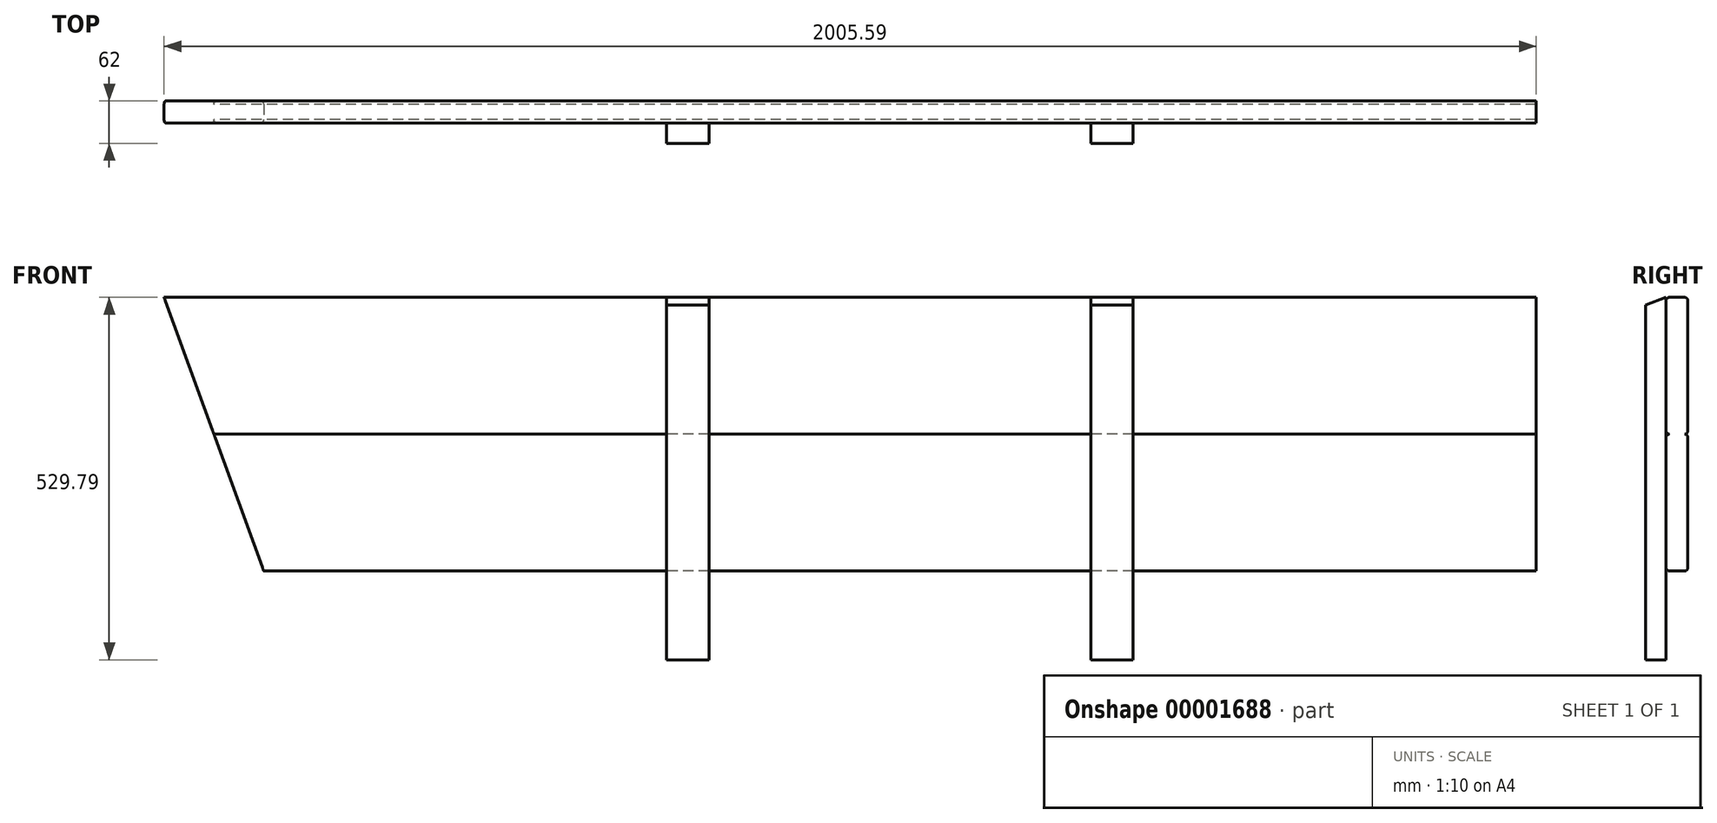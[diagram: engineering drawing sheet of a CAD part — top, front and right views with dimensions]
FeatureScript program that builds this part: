
annotation { "Feature Type Name" : "Feature", "Feature Type Description" : "" }
export const myFeature = defineFeature(function(context is Context, id is Id, definition is map)
    precondition{}
    {
        {
            var Q0;
            Q0=qCreatedBy(makeId("Right.planeOp"),FACE);
            var sketch = newSketch(context, id + "F0", { "sketchPlane" : qUnion([Q0])});
            skLineSegment(sketch, "E0.bottom", {"start": v(5, 0) * mm, "end": v(27, 0) * mm});
            skLineSegment(sketch, "E0.top", {"start": v(5, 200) * mm, "end": v(27, 200) * mm});
            skLineSegment(sketch, "E0.left", {"start": v(0, 5) * mm, "end": v(0, 195) * mm});
            skLineSegment(sketch, "E0.right", {"start": v(32, 5) * mm, "end": v(32, 195) * mm});
            skPoint(sketch, "E1.visualSharp", {"position": v(32, 200) * mm});
            skArc(sketch, "E1.filletArc", {"start": v(32, 195) * mm, "mid": v(30.54, 198.54) * mm, "end": v(27, 200) * mm});
            skPoint(sketch, "E2.visualSharp", {"position": v(0, 200) * mm});
            skArc(sketch, "E2.filletArc", {"start": v(5, 200) * mm, "mid": v(1.46, 198.54) * mm, "end": v(0, 195) * mm});
            skPoint(sketch, "E3.visualSharp", {"position": v(32, 0) * mm});
            skArc(sketch, "E3.filletArc", {"start": v(27, 0) * mm, "mid": v(30.54, 1.46) * mm, "end": v(32, 5) * mm});
            skPoint(sketch, "E4.visualSharp", {"position": v(0, 0) * mm});
            skArc(sketch, "E4.filletArc", {"start": v(0, 5) * mm, "mid": v(1.46, 1.46) * mm, "end": v(5, 0) * mm});
            skLineSegment(sketch, "E5.top", {"start": v(5, 400) * mm, "end": v(27, 400) * mm});
            skLineSegment(sketch, "E5.left", {"start": v(0, 205) * mm, "end": v(0, 395) * mm});
            skLineSegment(sketch, "E5.right", {"start": v(32, 205) * mm, "end": v(32, 395) * mm});
            skArc(sketch, "E6.filletArc", {"start": v(27, 200) * mm, "mid": v(30.54, 201.46) * mm, "end": v(32, 205) * mm});
            skArc(sketch, "E7.filletArc", {"start": v(0, 205) * mm, "mid": v(1.46, 201.46) * mm, "end": v(5, 200) * mm});
            skPoint(sketch, "E8.visualSharp", {"position": v(32, 400) * mm});
            skArc(sketch, "E8.filletArc", {"start": v(32, 395) * mm, "mid": v(30.54, 398.54) * mm, "end": v(27, 400) * mm});
            skPoint(sketch, "E9.visualSharp", {"position": v(0, 400) * mm});
            skArc(sketch, "E9.filletArc", {"start": v(5, 400) * mm, "mid": v(1.46, 398.54) * mm, "end": v(0, 395) * mm});
            skSolve(sketch);
        }
        {
            var Q0;
            Q0=makeQuery(id+"F0.imprint","IMPRINT",FACE,{"disambiguationData":[TD([[makeQuery(id+"F0.imprint","IMPRINT",EDGE,{"derivedFrom":sQuery(id+"F0.wireOp",EDGE,"E0.top")}),1.0]])]});
            var Q1;
            Q1=makeQuery(id+"F0.imprint","IMPRINT",FACE,{"disambiguationData":[TD([[makeQuery(id+"F0.imprint","IMPRINT",EDGE,{"derivedFrom":sQuery(id+"F0.wireOp",EDGE,"E0.bottom")}),1.0]])]});
            extrude(context, id + "F1", {"entities" : qUnion([Q0, Q1]), "depth" : 1860 * mm});
        }
        {
            var Q0;
            Q0=makeQuery(id+"F1.opExtrude","CAP_FACE",FACE,{"disambiguationData":[OSD([sQuery(id+"F0.wireOp",EDGE,"E0.bottom"),sQuery(id+"F0.wireOp",EDGE,"E0.left"),sQuery(id+"F0.wireOp",EDGE,"E0.right"),sQuery(id+"F0.wireOp",EDGE,"E1.filletArc"),sQuery(id+"F0.wireOp",EDGE,"E2.filletArc"),sQuery(id+"F0.wireOp",EDGE,"E3.filletArc"),sQuery(id+"F0.wireOp",EDGE,"E4.filletArc"),sQuery(id+"F0.wireOp",EDGE,"E5.top"),sQuery(id+"F0.wireOp",EDGE,"E5.left"),sQuery(id+"F0.wireOp",EDGE,"E5.right"),sQuery(id+"F0.wireOp",EDGE,"E6.filletArc"),sQuery(id+"F0.wireOp",EDGE,"E7.filletArc"),sQuery(id+"F0.wireOp",EDGE,"E8.filletArc"),sQuery(id+"F0.wireOp",EDGE,"E9.filletArc")])],"isStart":true});
            cPlane(context, id + "F2", {"entities" : qUnion([Q0]), "cplaneType" : CPlaneType.OFFSET, "offset" : 930 * mm, "oppositeDirection" : true, "width" : 150 * mm, "height" : 150 * mm});
        }
        {
            var Q0;
            Q0=makeQuery(id+"F1.opExtrude","SWEPT_FACE",FACE,{"disambiguationData":[OSD([sQuery(id+"F0.wireOp",EDGE,"E5.top")])]});
            var sketch = newSketch(context, id + "F3", { "sketchPlane" : qUnion([Q0])});
            skLineSegment(sketch, "E10.bottom", {"start": v(589, -30) * mm, "end": v(651, -30) * mm});
            skLineSegment(sketch, "E10.top", {"start": v(589, 0) * mm, "end": v(651, 0) * mm});
            skLineSegment(sketch, "E10.left", {"start": v(589, -30) * mm, "end": v(589, 0) * mm});
            skLineSegment(sketch, "E10.right", {"start": v(651, -30) * mm, "end": v(651, 0) * mm});
            skLineSegment(sketch, "E11", {"start": v(620, -30) * mm, "end": v(620, 0) * mm});
            skSolve(sketch);
        }
        {
            var Q0;
            {var subQ2=sQuery(id+"F3.wireOp",EDGE,"E10.left");var subQ7=sQuery(id+"F3.wireOp",EDGE,"E10.right");Q0=qUnion([makeQuery(id+"F3.imprint","IMPRINT",FACE,{"disambiguationData":[TD([[makeQuery(id+"F3.imprint","IMPRINT",EDGE,{"derivedFrom":subQ2}),-1.0]])]}),makeQuery(id+"F3.imprint","IMPRINT",FACE,{"disambiguationData":[TD([[makeQuery(id+"F3.imprint","IMPRINT",EDGE,{"derivedFrom":subQ7}),1.0]])]})]);}
            extrude(context, id + "F4", {"entities" : qUnion([Q0]), "oppositeDirection" : true, "depth" : 529.8 * mm});
        }
        {
            var Q0;
            Q0=makeQuery(id+"F4.opExtrude","SWEPT_FACE",FACE,{"disambiguationData":[OSD([sQuery(id+"F3.wireOp",EDGE,"E10.left")])]});
            var sketch = newSketch(context, id + "F5", { "sketchPlane" : qUnion([Q0])});
            skLineSegment(sketch, "E12", {"start": v(0, 400) * mm, "end": v(30, 389.08) * mm});
            skSolve(sketch);
        }
        {
            var Q0;
            Q0 = qSketchRegion(id + "F5", true);
            var Q1;
            {var subQ2=sQuery(id+"F5.wireOp",EDGE,"E12");Q1=makeQuery(id+"F5.imprint","IMPRINT",FACE,{"disambiguationData":[TD([[makeQuery(id+"F5.imprint","IMPRINT",EDGE,{"derivedFrom":subQ2}),1.0]])]});}
            extrude(context, id + "F6", {"entities" : qUnion([Q0, Q1]), "operationType" : NewBodyOperationType.REMOVE, "endBound" : BoundingType.THROUGH_ALL, "oppositeDirection" : true, "depth" : 25 * mm});
        }
        {
            var Q0;
            Q0=makeQuery(id+"F4.opExtrude","SWEPT_BODY",BODY,{"disambiguationData":[OSD([sQuery(id+"F3.wireOp",EDGE,"E10.bottom"),sQuery(id+"F3.wireOp",EDGE,"E10.top"),sQuery(id+"F3.wireOp",EDGE,"E10.left"),sQuery(id+"F3.wireOp",EDGE,"E10.right")])]});
            var Q1;
            Q1=qCreatedBy(id+"F2.planeOp",FACE);
            mirror(context, id + "F7", {"entities" : qUnion([Q0]), "mirrorPlane" : qUnion([Q1])});
        }
        {
            var Q0;
            Q0=makeQuery(id+"F1.opExtrude","CAP_FACE",FACE,{"disambiguationData":[OSD([sQuery(id+"F0.wireOp",EDGE,"E0.bottom"),sQuery(id+"F0.wireOp",EDGE,"E0.left"),sQuery(id+"F0.wireOp",EDGE,"E0.right"),sQuery(id+"F0.wireOp",EDGE,"E1.filletArc"),sQuery(id+"F0.wireOp",EDGE,"E2.filletArc"),sQuery(id+"F0.wireOp",EDGE,"E3.filletArc"),sQuery(id+"F0.wireOp",EDGE,"E4.filletArc"),sQuery(id+"F0.wireOp",EDGE,"E5.top"),sQuery(id+"F0.wireOp",EDGE,"E5.left"),sQuery(id+"F0.wireOp",EDGE,"E5.right"),sQuery(id+"F0.wireOp",EDGE,"E6.filletArc"),sQuery(id+"F0.wireOp",EDGE,"E7.filletArc"),sQuery(id+"F0.wireOp",EDGE,"E8.filletArc"),sQuery(id+"F0.wireOp",EDGE,"E9.filletArc")])],"isStart":true});
            extrude(context, id + "F8", {"entities" : qUnion([Q0]), "operationType" : NewBodyOperationType.ADD, "depth" : 500 * mm});
        }
        {
            var Q0;
            {var subQ0=sQuery(id+"F0.wireOp",EDGE,"E0.left");Q0=makeQuery(id+"F8.boolean.opBoolean","MERGE",FACE,{"derivedFrom":[makeQuery(id+"F1.opExtrude","SWEPT_FACE",FACE,{"disambiguationData":[OSD([subQ0])]}),makeQuery(id+"F8.opExtrude","SWEPT_FACE",FACE,{"disambiguationData":[OSD([subQ0])]})]});}
            var sketch = newSketch(context, id + "F9", { "sketchPlane" : qUnion([Q0])});
            skLineSegment(sketch, "E13", {"start": v(0, 0) * mm, "end": v(-280.45, 770.54) * mm});
            skLineSegment(sketch, "E14", {"start": v(-280.45, 770.54) * mm, "end": v(-958.61, 770.54) * mm});
            skLineSegment(sketch, "E15", {"start": v(-958.61, 770.54) * mm, "end": v(-958.61, 0) * mm});
            skLineSegment(sketch, "E16", {"start": v(-958.61, 0) * mm, "end": v(0, 0) * mm});
            skSolve(sketch);
        }
        {
            var Q0;
            {var subQ0=sQuery(id+"F0.wireOp",EDGE,"E0.left");var subQ5=makeQuery(id+"F8.opExtrude","CAP_EDGE",EDGE,{"disambiguationData":[OSD([subQ0])],"isStart":false});var subQ7=makeQuery(id+"F9.imprint","IMPRINT",EDGE,{"derivedFrom":subQ5});var subQ13=sQuery(id+"F9.wireOp",EDGE,"E14");Q0=qUnion([makeQuery(id+"F9.imprint","IMPRINT",FACE,{"disambiguationData":[TD([[makeQuery(id+"F9.imprint","IMPRINT",EDGE,{"derivedFrom":subQ13}),1.0]])]}),makeQuery(id+"F9.imprint","IMPRINT",FACE,{"disambiguationData":[TD([[subQ7,-1.0]])]})]);}
            extrude(context, id + "F10", {"entities" : qUnion([Q0]), "operationType" : NewBodyOperationType.REMOVE, "endBound" : BoundingType.THROUGH_ALL, "oppositeDirection" : true, "depth" : 25 * mm});
        }
    });
